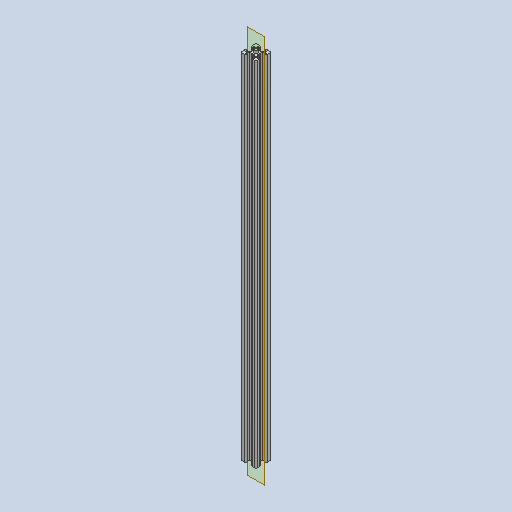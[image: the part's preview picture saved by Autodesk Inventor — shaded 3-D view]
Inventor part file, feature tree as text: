
AUTODESK INVENTOR PART (.ipt)
format: ipt  version: 2025.2 (Build 292293000, 293)  size: 407,552 bytes
history: native  units: mm
features: other x1, extrude x1, sketch x1
ambient origin geometry x8: Origin, YZ Plane, XZ Plane, XY Plane, X Axis, Y Axis, Z Axis, Center Point
bodies: Body1 (feature_tree)
feature tree (3):
  other  "Твердое тело1"
  extrude  "Выдавливание1"  Depth=0.25mm
  sketch  "Эскиз1"
